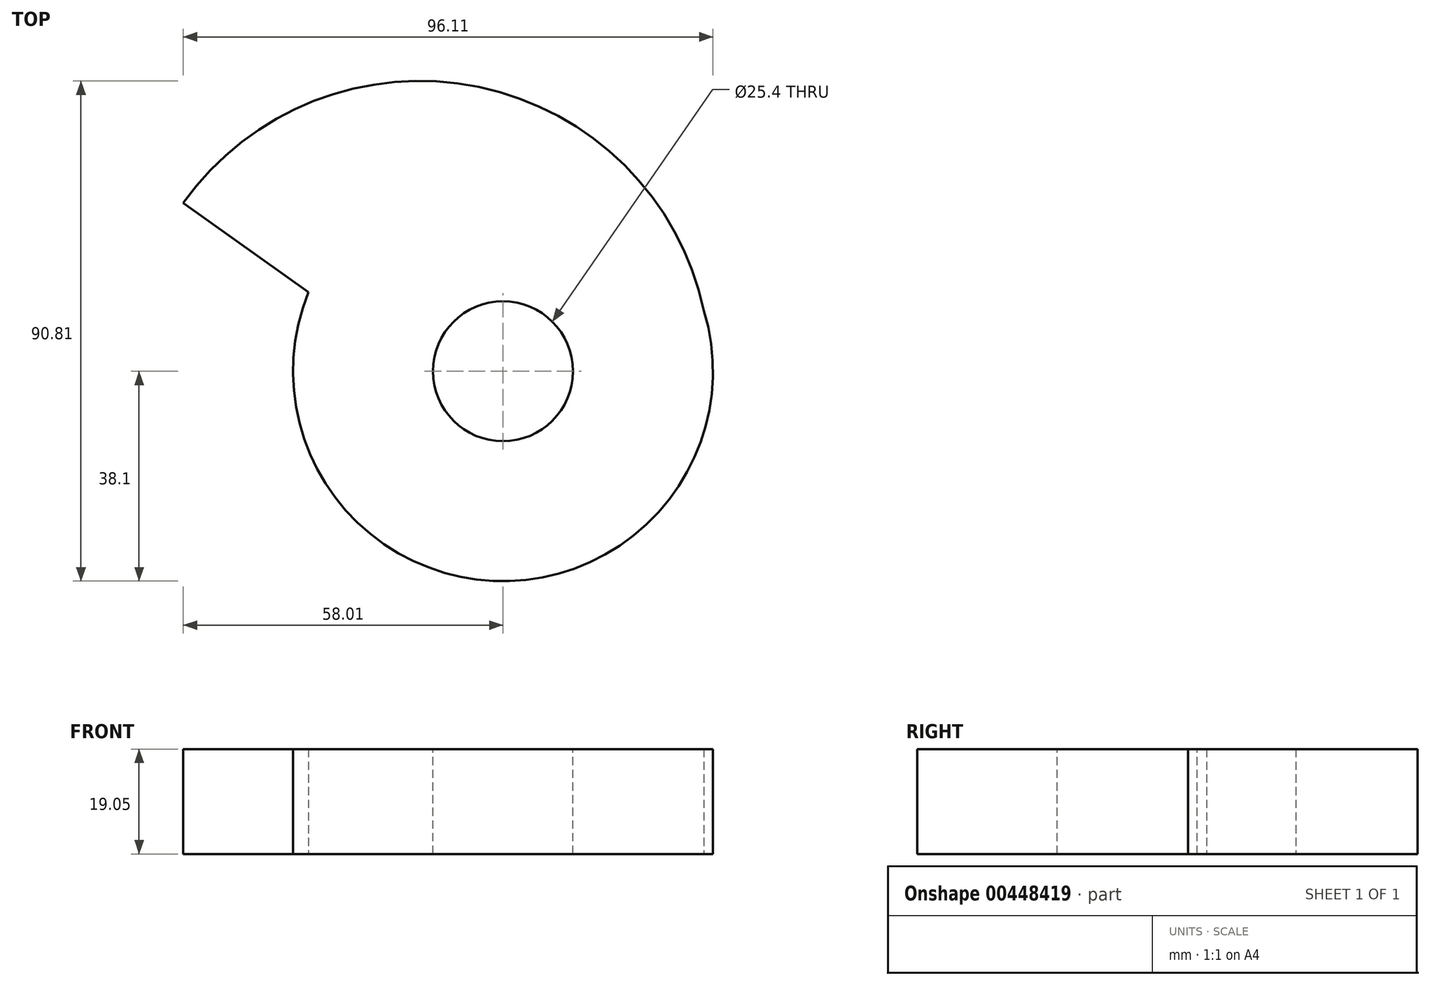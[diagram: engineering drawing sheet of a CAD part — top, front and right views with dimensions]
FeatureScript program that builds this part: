
annotation { "Feature Type Name" : "Feature", "Feature Type Description" : "" }
export const myFeature = defineFeature(function(context is Context, id is Id, definition is map)
    precondition{}
    {
        {
            var Q0;
            Q0=qCreatedBy(makeId("Top.planeOp"),FACE);
            var sketch = newSketch(context, id + "F0", { "sketchPlane" : qUnion([Q0])});
            skArc(sketch, "E0", {"start": v(-35.28, 14.4) * mm, "mid": v(-1.8, -38.06) * mm, "end": v(36.47, 11.01) * mm});
            skArc(sketch, "E1", {"start": v(36.47, 11.01) * mm, "mid": v(-4.39, 51.62) * mm, "end": v(-58.01, 30.58) * mm});
            skLineSegment(sketch, "E2", {"start": v(-58.01, 30.58) * mm, "end": v(-35.28, 14.4) * mm});
            skSolve(sketch);
        }
        {
            var Q0;
            Q0 = qSketchRegion(id + "F0", true);
            extrude(context, id + "F1", {"entities" : qUnion([Q0]), "depth" : 19.05 * mm});
        }
        {
            var Q0;
            Q0=makeQuery(id+"F1.opExtrude","CAP_FACE",FACE,{"disambiguationData":[OSD([sQuery(id+"F0.wireOp",EDGE,"E0"),sQuery(id+"F0.wireOp",EDGE,"E1"),sQuery(id+"F0.wireOp",EDGE,"E2")])],"isStart":false});
            var sketch = newSketch(context, id + "F2", { "sketchPlane" : qUnion([Q0])});
            skCircle(sketch, "E3", {"center": v(0, 0) * mm, "radius": 12.7 * mm});
            skSolve(sketch);
        }
        {
            var Q0;
            Q0 = qSketchRegion(id + "F2", true);
            extrude(context, id + "F3", {"entities" : qUnion([Q0]), "operationType" : NewBodyOperationType.REMOVE, "oppositeDirection" : true, "depth" : 25.4 * mm});
        }
    });
